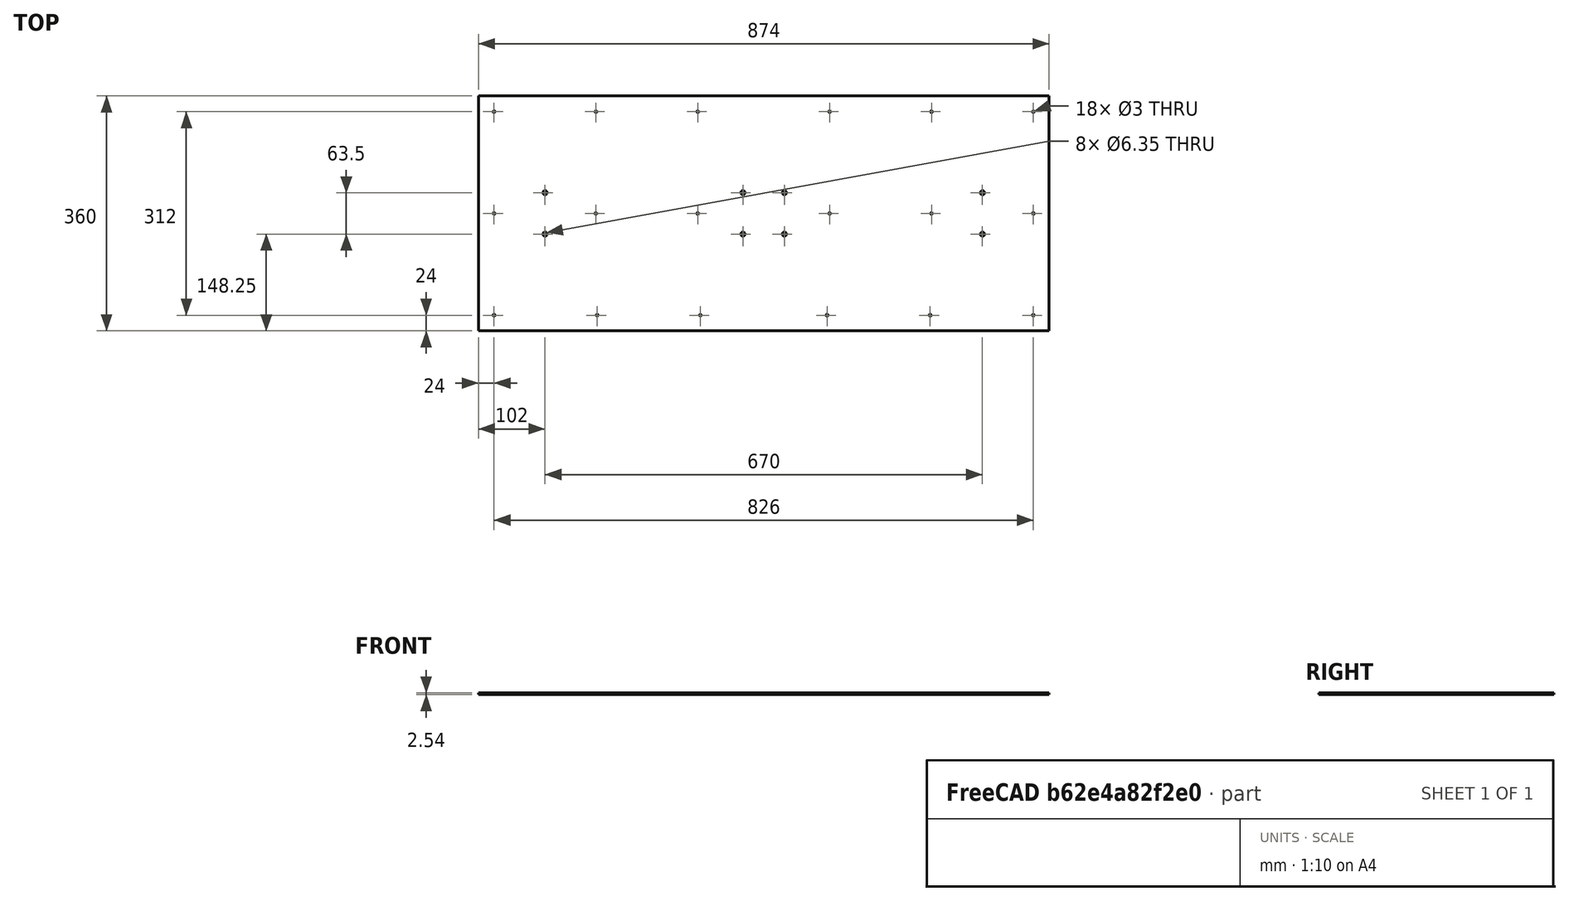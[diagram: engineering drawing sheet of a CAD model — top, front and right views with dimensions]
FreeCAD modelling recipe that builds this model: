
FCSTD DOCUMENT  (FreeCAD 0.21R33771 (Git))
Label: panel2_v2
License: All rights reserved
LicenseURL: https://en.wikipedia.org/wiki/All_rights_reserved
objects: Sketcher::SketchObject×2, PartDesign::Pad×1, PartDesign::Body×1
note: 5 computed .brp shape members not serialized (recipe doc carries the construction recipe); baked Part::Feature solids carry a one-line shape summary decoded from their .brp

FEATURE [Sketcher::SketchObject] Sketch
  FullyConstrained = false
  MapMode = 2
  sketch-geometry (31):
    g0: LineSegment StartX=-437 StartY=180 StartZ=0 EndX=437 EndY=180 EndZ=0
    g1: LineSegment StartX=437 StartY=180 StartZ=0 EndX=437 EndY=-180 EndZ=0
    g2: LineSegment StartX=437 StartY=-180 StartZ=0 EndX=-437 EndY=-180 EndZ=0
    g3: LineSegment StartX=-437 StartY=-180 StartZ=0 EndX=-437 EndY=180 EndZ=0
    g4: Circle CenterX=-413 CenterY=-1.02831e-05 CenterZ=0 NormalX=0 NormalY=0 NormalZ=1 AngleXU=0 Radius=1.5
    g5: Circle CenterX=-413 CenterY=-156 CenterZ=0 NormalX=0 NormalY=0 NormalZ=1 AngleXU=0 Radius=1.5
    g6: Circle CenterX=-335 CenterY=31.75 CenterZ=0 NormalX=0 NormalY=0 NormalZ=1 AngleXU=0 Radius=3.175
    g7: Circle CenterX=-257 CenterY=156 CenterZ=0 NormalX=0 NormalY=0 NormalZ=1 AngleXU=0 Radius=1.4986
    g8: Circle CenterX=-335 CenterY=-31.75 CenterZ=0 NormalX=0 NormalY=0 NormalZ=1 AngleXU=0 Radius=3.175
    g9: Circle CenterX=-257 CenterY=0 CenterZ=0 NormalX=0 NormalY=0 NormalZ=1 AngleXU=0 Radius=1.5
    g10: Circle CenterX=-255 CenterY=-156 CenterZ=0 NormalX=0 NormalY=0 NormalZ=1 AngleXU=0 Radius=1.5
    g11: Circle CenterX=-101 CenterY=156 CenterZ=0 NormalX=0 NormalY=0 NormalZ=1 AngleXU=0 Radius=1.5
    g12: Circle CenterX=-101 CenterY=0 CenterZ=0 NormalX=0 NormalY=0 NormalZ=1 AngleXU=0 Radius=1.5
    g13: Circle CenterX=-97 CenterY=-156 CenterZ=0 NormalX=0 NormalY=0 NormalZ=1 AngleXU=0 Radius=1.5
    g14: LineSegment StartX=0 StartY=180 StartZ=0 EndX=0 EndY=-180 EndZ=0
    g15: Circle CenterX=413 CenterY=156 CenterZ=0 NormalX=0 NormalY=0 NormalZ=1 AngleXU=0 Radius=1.5
    g16: Circle CenterX=413 CenterY=-1.21668e-11 CenterZ=0 NormalX=0 NormalY=0 NormalZ=1 AngleXU=0 Radius=1.5
    g17: Circle CenterX=413 CenterY=-156 CenterZ=0 NormalX=0 NormalY=0 NormalZ=1 AngleXU=0 Radius=1.5
    g18: Circle CenterX=335 CenterY=31.75 CenterZ=0 NormalX=0 NormalY=0 NormalZ=1 AngleXU=0 Radius=3.175
    g19: Circle CenterX=257 CenterY=156 CenterZ=0 NormalX=0 NormalY=0 NormalZ=1 AngleXU=0 Radius=1.5
    g20: Circle CenterX=335 CenterY=-31.75 CenterZ=0 NormalX=0 NormalY=0 NormalZ=1 AngleXU=0 Radius=3.175
    g21: Circle CenterX=257 CenterY=0 CenterZ=0 NormalX=0 NormalY=0 NormalZ=1 AngleXU=0 Radius=1.5
    g22: Circle CenterX=255 CenterY=-156 CenterZ=0 NormalX=0 NormalY=0 NormalZ=1 AngleXU=0 Radius=1.5
    g23: Circle CenterX=101 CenterY=156 CenterZ=0 NormalX=0 NormalY=0 NormalZ=1 AngleXU=0 Radius=1.5
    g24: Circle CenterX=101 CenterY=0 CenterZ=0 NormalX=0 NormalY=0 NormalZ=1 AngleXU=0 Radius=1.5
    g25: Circle CenterX=97 CenterY=-156 CenterZ=0 NormalX=0 NormalY=0 NormalZ=1 AngleXU=0 Radius=1.5
    g26: Circle CenterX=-31.75 CenterY=31.75 CenterZ=0 NormalX=0 NormalY=0 NormalZ=1 AngleXU=0 Radius=3.175
    g27: Circle CenterX=-31.75 CenterY=-31.75 CenterZ=0 NormalX=0 NormalY=0 NormalZ=1 AngleXU=0 Radius=3.175
    g28: Circle CenterX=31.75 CenterY=31.75 CenterZ=0 NormalX=0 NormalY=0 NormalZ=1 AngleXU=0 Radius=3.175
    g29: Circle CenterX=31.75 CenterY=-31.75 CenterZ=0 NormalX=0 NormalY=0 NormalZ=1 AngleXU=0 Radius=3.175
    g30: Circle CenterX=-413 CenterY=156 CenterZ=0 NormalX=0 NormalY=0 NormalZ=1 AngleXU=0 Radius=1.4986
  constraints (65):
    c: Coincident(g0,g1)
    c: Coincident(g1,g2)
    c: Coincident(g2,g3)
    c: Coincident(g3,g0)
    c: Horizontal(g0)
    c: Horizontal(g2)
    c: Vertical(g1)
    c: DistanceX(g0,g0) = 874
    c: DistanceY(g1,g1) = 360
    c: Diameter(g4) = 3
    c: Diameter(g5) = 3
    c: Diameter(g6) = 6.35
    c: Diameter(g7) = 2.9972
    c: Diameter(g8) = 6.35
    c: Distance(g4,g3) = 24
    c: Distance(g5,g3) = 24
    c: Diameter(g9) = 3
    c: Diameter(g10) = 3
    c: Distance(g4,g5) = 156
    c: DistanceX(g4,g8) = 78
    c: DistanceX(g6,g9) = 78
    c: Distance(g7,g0) = 24
    c: DistanceX(g5,g10) = 158
    c: Distance(g10,g2) = 24
    c: Diameter(g11) = 3
    c: Diameter(g12) = 3
    c: Diameter(g13) = 3
    c: DistanceX(g7,g11) = 156
    c: Distance(g11,g0) = 24
    c: DistanceX(g4,g6) = 78
    c: DistanceX(g9,g12) = 156
    c: DistanceX(g10,g13) = 158
    c: Distance(g13,g2) = 24
    c: PointOnObject(g14,g0)
    c: PointOnObject(g14,g2)
    c: Vertical(g14)
    c: DistanceX(g14,g0) = 437
    c: Symmetric(g0,g2,g-1)
    c: Distance(g6,g-1) = 31.75
    c: Distance(g8,g-1) = 31.75
    c: PointOnObject(g9,g-1)
    c: PointOnObject(g12,g-1)
    c: PointOnObject(g-1,g14)
    c: Diameter(g15) = 3
    c: Diameter(g16) = 3
    c: Diameter(g17) = 3
    c: Diameter(g18) = 6.35
    c: Diameter(g19) = 3
    c: Diameter(g20) = 6.35
    c: Distance(g15,g16) = 156
    c: Diameter(g21) = 3
    c: Diameter(g22) = 3
    c: Distance(g16,g17) = 156
    c: Diameter(g23) = 3
    c: Diameter(g24) = 3
    c: Diameter(g25) = 3
    c: Diameter(g26) = 6.35
    c: Distance(g26,g-1) = 31.75
    c: Distance(g26,g14) = 31.75
    c: Diameter(g27) = 6.35
    c: Diameter(g28) = 6.35
    c: Diameter(g29) = 6.35
    c: Diameter(g30) = 2.9972
    c: Distance(g30,g3) = 24
    c: Distance(g30,g0) = 24
FEATURE [PartDesign::Pad] Pad
  Direction = (0,0,1)
  Length = 2.54
  Length2 = 10
  Profile = -> Sketch
  ReferenceAxis = -> Sketch [N_Axis]
  Type = 0
FEATURE [Sketcher::SketchObject] Sketch005
  FullyConstrained = false
  MapMode = 5
  Placement = pos=(0,0,2.54) rot=(0,0,1;0rad)
  sketch-geometry (1):
    g0: Circle CenterX=-202.559 CenterY=109.81 CenterZ=0 NormalX=0 NormalY=0 NormalZ=1 AngleXU=0 Radius=48.0866
FEATURE [PartDesign::Body] Body
  Group = -> [Sketch,Pad,Sketch005]
  Origin = -> Origin001
  Tip = -> Pad
